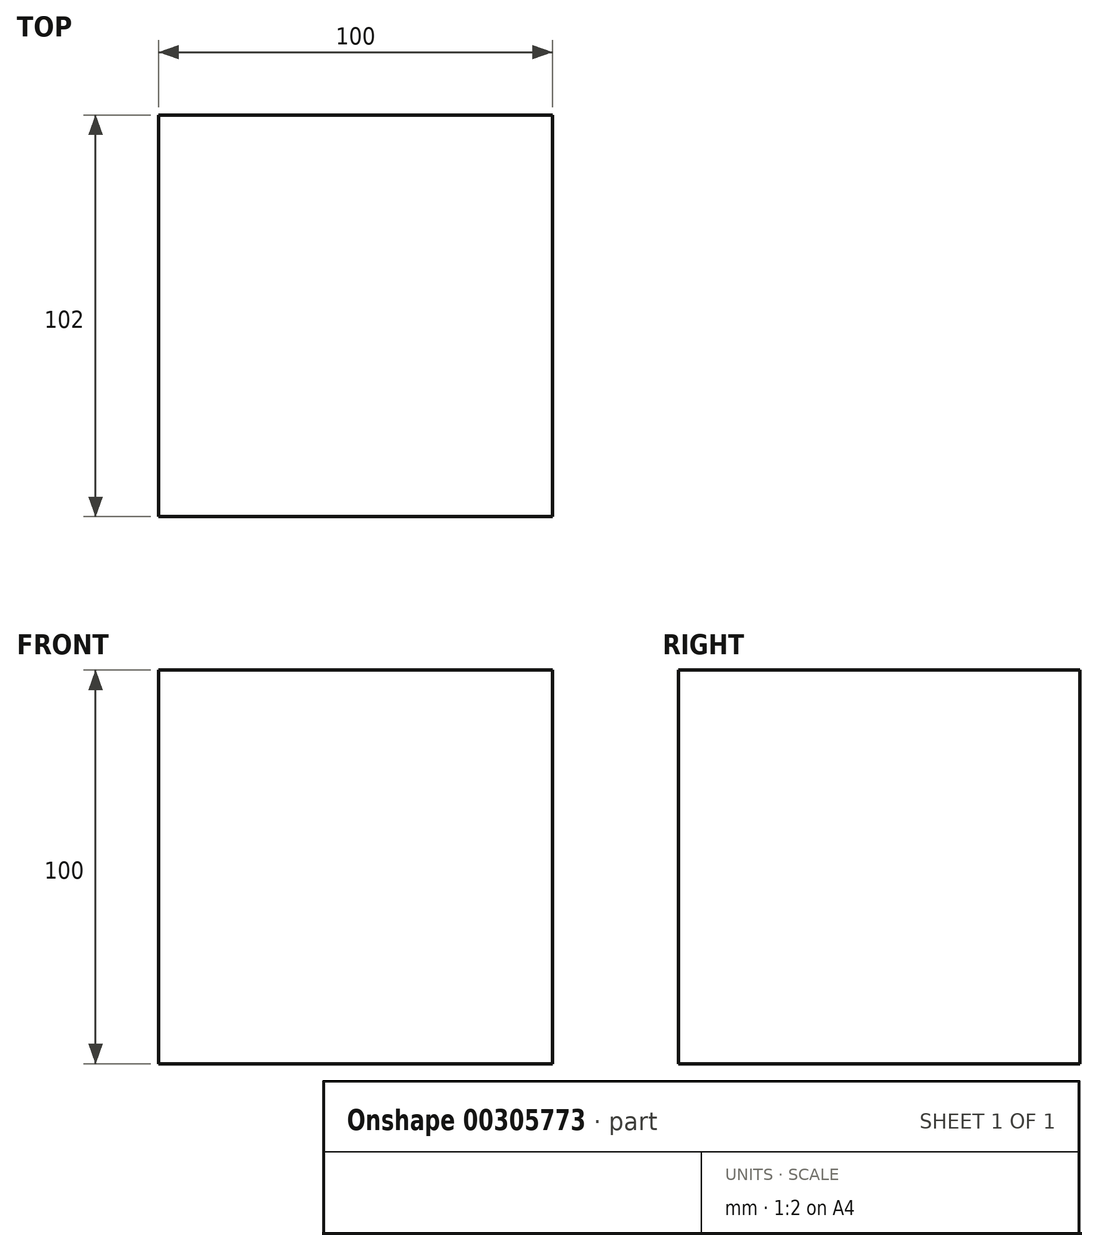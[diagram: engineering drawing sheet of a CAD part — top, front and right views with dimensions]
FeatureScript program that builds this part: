
annotation { "Feature Type Name" : "Feature", "Feature Type Description" : "" }
export const myFeature = defineFeature(function(context is Context, id is Id, definition is map)
    precondition{}
    {
        {
            var Q0;
            Q0=qCreatedBy(makeId("Top.planeOp"),FACE);
            var sketch = newSketch(context, id + "F0", { "sketchPlane" : qUnion([Q0])});
            skLineSegment(sketch, "E0.bottom", {"start": v(-62.05, 52.34) * mm, "end": v(37.95, 52.34) * mm});
            skLineSegment(sketch, "E0.top", {"start": v(-62.05, -49.66) * mm, "end": v(37.95, -49.66) * mm});
            skLineSegment(sketch, "E0.left", {"start": v(-62.05, 52.34) * mm, "end": v(-62.05, -49.66) * mm});
            skLineSegment(sketch, "E0.right", {"start": v(37.95, 52.34) * mm, "end": v(37.95, -49.66) * mm});
            skSolve(sketch);
        }
        {
            var Q0;
            Q0 = qSketchRegion(id + "F0", true);
            extrude(context, id + "F1", {"entities" : qUnion([Q0]), "depth" : 100 * mm});
        }
    });
